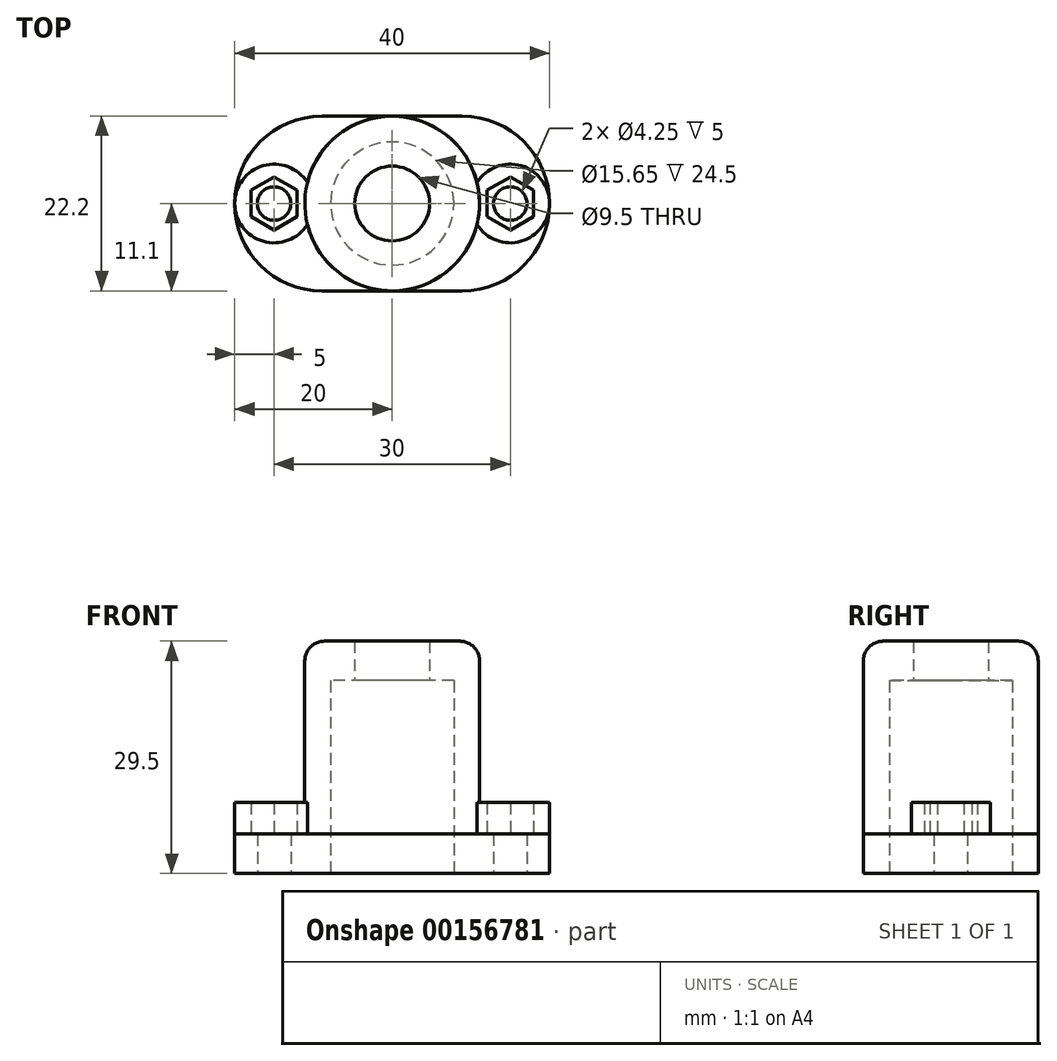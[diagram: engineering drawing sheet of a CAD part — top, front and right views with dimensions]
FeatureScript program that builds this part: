
annotation { "Feature Type Name" : "Feature", "Feature Type Description" : "" }
export const myFeature = defineFeature(function(context is Context, id is Id, definition is map)
    precondition{}
    {
        {
            var Q0;
            Q0=qCreatedBy(makeId("Top.planeOp"),FACE);
            var sketch = newSketch(context, id + "F0", { "sketchPlane" : qUnion([Q0])});
            skCircle(sketch, "E0", {"center": v(0, 0) * mm, "radius": 7.83 * mm});
            skLineSegment(sketch, "E1.bottom", {"start": v(20, -11.1) * mm, "end": v(-20, -11.1) * mm});
            skLineSegment(sketch, "E1.top", {"start": v(20, 11.1) * mm, "end": v(-20, 11.1) * mm});
            skLineSegment(sketch, "E1.left", {"start": v(20, -11.1) * mm, "end": v(20, 11.1) * mm});
            skLineSegment(sketch, "E1.right", {"start": v(-20, -11.1) * mm, "end": v(-20, 11.1) * mm});
            skCircle(sketch, "E2", {"center": v(-15, 0) * mm, "radius": 2.12 * mm});
            skCircle(sketch, "E3.MirrorC", {"center": v(15, 0) * mm, "radius": 2.12 * mm});
            skSolve(sketch);
        }
        {
            var Q0;
            Q0=qSketchRegion(id+"F0",true);
            extrude(context, id + "F1", {"entities" : qUnion([Q0]), "depth" : 5 * mm});
        }
        {
            var Q0;
            Q0=makeQuery(id+"F1.opExtrude","CAP_FACE",FACE,{"disambiguationData":[OSD([sQuery(id+"F0.wireOp",EDGE,"E0"),sQuery(id+"F0.wireOp",EDGE,"E1.bottom"),sQuery(id+"F0.wireOp",EDGE,"E1.top"),sQuery(id+"F0.wireOp",EDGE,"E1.left"),sQuery(id+"F0.wireOp",EDGE,"E1.right")])],"isStart":false});
            var sketch = newSketch(context, id + "F2", { "sketchPlane" : qUnion([Q0])});
            skCircle(sketch, "E4", {"center": v(0, 0) * mm, "radius": 11.1 * mm});
            skCircle(sketch, "E5", {"center": v(0, 0) * mm, "radius": 7.83 * mm});
            skSolve(sketch);
        }
        {
            var Q0;
            Q0=qSketchRegion(id+"F2",true);
            extrude(context, id + "F3", {"entities" : qUnion([Q0]), "operationType" : NewBodyOperationType.ADD, "depth" : 19.5 * mm});
        }
        {
            var Q0;
            Q0=makeQuery(id+"F3.opExtrude","CAP_FACE",FACE,{"disambiguationData":[OSD([sQuery(id+"F2.wireOp",EDGE,"E4"),sQuery(id+"F2.wireOp",EDGE,"E5")])],"isStart":false});
            var sketch = newSketch(context, id + "F4", { "sketchPlane" : qUnion([Q0])});
            skCircle(sketch, "E6", {"center": v(0, 0) * mm, "radius": 4.75 * mm});
            skCircle(sketch, "E7", {"center": v(0, 0) * mm, "radius": 11.1 * mm});
            skSolve(sketch);
        }
        {
            var Q0;
            Q0=qSketchRegion(id+"F4",true);
            extrude(context, id + "F5", {"entities" : qUnion([Q0]), "operationType" : NewBodyOperationType.ADD, "depth" : 5 * mm});
        }
        {
            var Q0;
            Q0=makeQuery(id+"F1.opExtrude","SWEPT_EDGE",EDGE,{"disambiguationData":[OSD([sQuery(id+"F0.wireOp",EDGE,"E1.top"),sQuery(id+"F0.wireOp",EDGE,"E1.right")])]});
            var Q1;
            Q1=makeQuery(id+"F1.opExtrude","SWEPT_EDGE",EDGE,{"disambiguationData":[OSD([sQuery(id+"F0.wireOp",EDGE,"E1.bottom"),sQuery(id+"F0.wireOp",EDGE,"E1.right")])]});
            var Q2;
            Q2=makeQuery(id+"F1.opExtrude","SWEPT_EDGE",EDGE,{"disambiguationData":[OSD([sQuery(id+"F0.wireOp",EDGE,"E1.bottom"),sQuery(id+"F0.wireOp",EDGE,"E1.left")])]});
            var Q3;
            Q3=makeQuery(id+"F1.opExtrude","SWEPT_EDGE",EDGE,{"disambiguationData":[OSD([sQuery(id+"F0.wireOp",EDGE,"E1.top"),sQuery(id+"F0.wireOp",EDGE,"E1.left")])]});
            fillet(context, id + "F6", {"entities" : qUnion([Q0, Q1, Q2, Q3]), "radius" : 11.1 * mm, "tangentPropagation" : true, "allowEdgeOverflow" : false});
        }
        {
            var Q0;
            Q0=makeQuery(id+"F5.opExtrude","CAP_EDGE",EDGE,{"disambiguationData":[OSD([sQuery(id+"F4.wireOp",EDGE,"E7")])],"isStart":false});
            fillet(context, id + "F7", {"entities" : qUnion([Q0]), "radius" : 2.5 * mm, "tangentPropagation" : true, "allowEdgeOverflow" : false});
        }
        {
            var Q0;
            {var subQ0=sQuery(id+"F0.wireOp",EDGE,"E1.left");var subQ1=sQuery(id+"F0.wireOp",EDGE,"E1.top");var subQ2=sQuery(id+"F0.wireOp",EDGE,"E1.bottom");var subQ3=sQuery(id+"F0.wireOp",EDGE,"E3.MirrorC");var subQ4=makeQuery(id+"F1.opExtrude","CAP_FACE",FACE,{"disambiguationData":[OSD([sQuery(id+"F0.wireOp",EDGE,"E0"),subQ2,subQ1,subQ0,sQuery(id+"F0.wireOp",EDGE,"E1.right"),sQuery(id+"F0.wireOp",EDGE,"E2"),subQ3])],"isStart":false});Q0=makeQuery(id+"F3.boolean.opBoolean","SPLIT",FACE,{"disambiguationData":[TD([makeQuery(id+"F1.opExtrude","SWEPT_FACE",FACE,{"disambiguationData":[OSD([subQ0])]})])],"derivedFrom":subQ4});}
            var sketch = newSketch(context, id + "F8", { "sketchPlane" : qUnion([Q0])});
            skCircle(sketch, "E8.cCircle", {"center": v(-15, 0) * mm, "radius": 2.93 * mm, "construction": true});
            skLineSegment(sketch, "E8.0", {"start": v(-12.07, 1.69) * mm, "end": v(-12.07, -1.69) * mm});
            skLineSegment(sketch, "E8.1", {"start": v(-12.08, -1.69) * mm, "end": v(-15, -3.38) * mm});
            skLineSegment(sketch, "E8.2", {"start": v(-15, -3.38) * mm, "end": v(-17.93, -1.69) * mm});
            skLineSegment(sketch, "E8.3", {"start": v(-17.93, -1.69) * mm, "end": v(-17.93, 1.69) * mm});
            skLineSegment(sketch, "E8.4", {"start": v(-17.93, 1.69) * mm, "end": v(-15, 3.38) * mm});
            skLineSegment(sketch, "E8.5", {"start": v(-15, 3.38) * mm, "end": v(-12.07, 1.69) * mm});
            skPoint(sketch, "E8.0.midPoint", {"position": v(-12.07, 0) * mm});
            skCircle(sketch, "E9", {"center": v(-15, 0) * mm, "radius": 5 * mm});
            skPoint(sketch, "E10.MirrorP", {"position": v(12.07, 0) * mm});
            skCircle(sketch, "E11.MirrorC", {"center": v(15, 0) * mm, "radius": 2.93 * mm, "construction": true});
            skLineSegment(sketch, "E12.MirrorCS", {"start": v(12.07, 1.69) * mm, "end": v(12.07, -1.69) * mm});
            skLineSegment(sketch, "E13.MirrorCS", {"start": v(12.08, -1.69) * mm, "end": v(15, -3.38) * mm});
            skLineSegment(sketch, "E14.MirrorCS", {"start": v(15, -3.38) * mm, "end": v(17.93, -1.69) * mm});
            skLineSegment(sketch, "E15.MirrorCS", {"start": v(17.93, -1.69) * mm, "end": v(17.93, 1.69) * mm});
            skLineSegment(sketch, "E16.MirrorCS", {"start": v(17.93, 1.69) * mm, "end": v(15, 3.38) * mm});
            skLineSegment(sketch, "E17.MirrorCS", {"start": v(15, 3.38) * mm, "end": v(12.07, 1.69) * mm});
            skCircle(sketch, "E18.MirrorC", {"center": v(15, 0) * mm, "radius": 5 * mm});
            skSolve(sketch);
        }
        {
            var Q0;
            Q0 = qSketchRegion(id + "F8", true);
            extrude(context, id + "F9", {"entities" : qUnion([Q0]), "operationType" : NewBodyOperationType.ADD, "depth" : 4 * mm});
        }
    });
